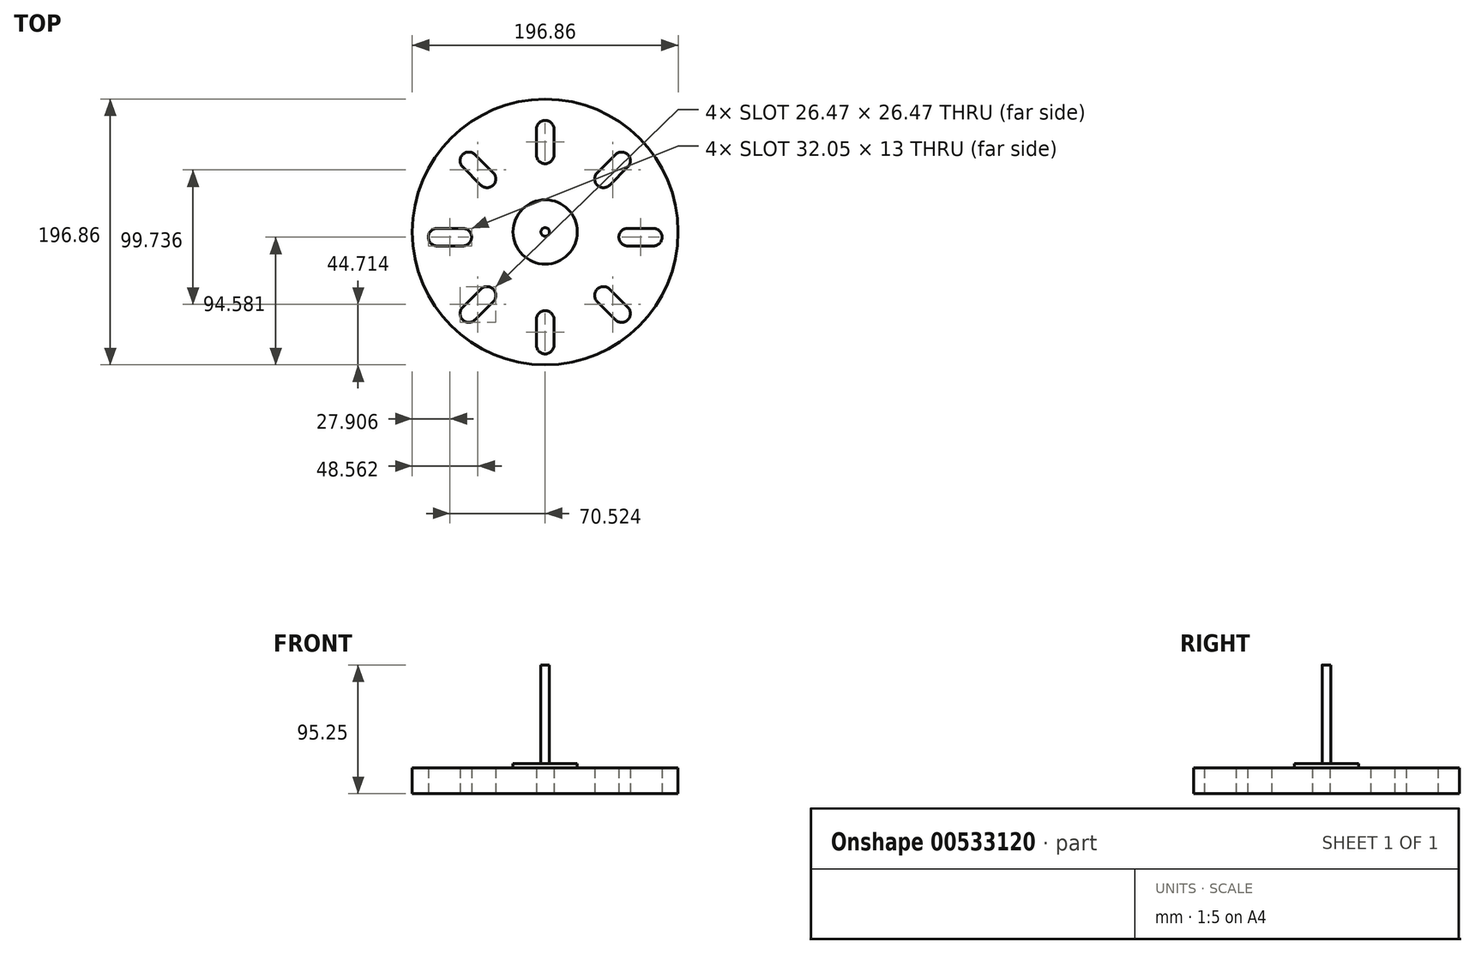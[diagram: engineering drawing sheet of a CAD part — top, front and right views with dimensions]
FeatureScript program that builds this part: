
annotation { "Feature Type Name" : "Feature", "Feature Type Description" : "" }
export const myFeature = defineFeature(function(context is Context, id is Id, definition is map)
    precondition{}
    {
        {
            var Q0;
            Q0=qCreatedBy(makeId("Top.planeOp"),FACE);
            var sketch = newSketch(context, id + "F0", { "sketchPlane" : qUnion([Q0])});
            skCircle(sketch, "E0", {"center": v(0, 0) * mm, "radius": 20.64 * mm});
            skCircle(sketch, "E1", {"center": v(0, 0) * mm, "radius": 98.43 * mm});
            skCircle(sketch, "E2", {"center": v(0, 0) * mm, "radius": 66.68 * mm, "construction": true});
            skPoint(sketch, "E3.center", {"position": v(-3.85, -3.85) * mm});
            skLineSegment(sketch, "E4", {"start": v(0, 57.15) * mm, "end": v(0, 76.2) * mm});
            skLineSegment(sketch, "E5.1.0", {"start": v(-43.13, 39.28) * mm, "end": v(-56.6, 52.75) * mm});
            skLineSegment(sketch, "E5.2.0", {"start": v(-61, -3.85) * mm, "end": v(-80.05, -3.85) * mm});
            skLineSegment(sketch, "E5.3.0", {"start": v(-43.13, -46.98) * mm, "end": v(-56.6, -60.45) * mm});
            skLineSegment(sketch, "E5.4.0", {"start": v(0, -64.85) * mm, "end": v(0, -83.9) * mm});
            skLineSegment(sketch, "E5.5.0", {"start": v(43.13, -46.98) * mm, "end": v(56.6, -60.45) * mm});
            skLineSegment(sketch, "E5.6.0", {"start": v(61, -3.85) * mm, "end": v(80.05, -3.85) * mm});
            skLineSegment(sketch, "E5.7.0", {"start": v(43.13, 39.28) * mm, "end": v(56.6, 52.75) * mm});
            skPoint(sketch, "E5.center", {"position": v(0, -3.85) * mm});
            skArc(sketch, "E6.0.startCap", {"start": v(6.5, 57.15) * mm, "mid": v(0, 50.65) * mm, "end": v(-6.5, 57.15) * mm});
            skArc(sketch, "E6.0.endCap", {"start": v(-6.5, 76.2) * mm, "mid": v(0, 82.7) * mm, "end": v(6.5, 76.2) * mm});
            skLineSegment(sketch, "E6.0.left", {"start": v(-6.5, 57.15) * mm, "end": v(-6.5, 76.2) * mm});
            skLineSegment(sketch, "E6.0.right", {"start": v(6.5, 57.15) * mm, "end": v(6.5, 76.2) * mm});
            skArc(sketch, "E6.1.startCap", {"start": v(47.73, 34.69) * mm, "mid": v(38.54, 34.69) * mm, "end": v(38.54, 43.88) * mm});
            skArc(sketch, "E6.1.endCap", {"start": v(52, 57.35) * mm, "mid": v(61.2, 57.35) * mm, "end": v(61.2, 48.16) * mm});
            skLineSegment(sketch, "E6.1.left", {"start": v(38.54, 43.88) * mm, "end": v(52, 57.35) * mm});
            skLineSegment(sketch, "E6.1.right", {"start": v(47.73, 34.69) * mm, "end": v(61.2, 48.16) * mm});
            skArc(sketch, "E6.2.startCap", {"start": v(47.73, 34.69) * mm, "mid": v(38.54, 34.69) * mm, "end": v(38.54, 43.88) * mm});
            skArc(sketch, "E6.2.endCap", {"start": v(52, 57.35) * mm, "mid": v(61.2, 57.35) * mm, "end": v(61.2, 48.16) * mm});
            skLineSegment(sketch, "E6.2.left", {"start": v(38.54, 43.88) * mm, "end": v(52, 57.35) * mm});
            skLineSegment(sketch, "E6.2.right", {"start": v(47.73, 34.69) * mm, "end": v(61.2, 48.16) * mm});
            skArc(sketch, "E6.3.startCap", {"start": v(61, -10.35) * mm, "mid": v(54.5, -3.85) * mm, "end": v(61, 2.65) * mm});
            skArc(sketch, "E6.3.endCap", {"start": v(80.05, 2.65) * mm, "mid": v(86.55, -3.85) * mm, "end": v(80.05, -10.35) * mm});
            skLineSegment(sketch, "E6.3.left", {"start": v(61, 2.65) * mm, "end": v(80.05, 2.65) * mm});
            skLineSegment(sketch, "E6.3.right", {"start": v(61, -10.35) * mm, "end": v(80.05, -10.35) * mm});
            skArc(sketch, "E6.4.startCap", {"start": v(38.54, -51.58) * mm, "mid": v(38.54, -42.39) * mm, "end": v(47.73, -42.39) * mm});
            skArc(sketch, "E6.4.endCap", {"start": v(61.2, -55.86) * mm, "mid": v(61.2, -65.05) * mm, "end": v(52, -65.05) * mm});
            skLineSegment(sketch, "E6.4.left", {"start": v(47.73, -42.39) * mm, "end": v(61.2, -55.86) * mm});
            skLineSegment(sketch, "E6.4.right", {"start": v(38.54, -51.58) * mm, "end": v(52, -65.05) * mm});
            skArc(sketch, "E6.5.startCap", {"start": v(-6.5, -64.85) * mm, "mid": v(0, -58.35) * mm, "end": v(6.5, -64.85) * mm});
            skArc(sketch, "E6.5.endCap", {"start": v(6.5, -83.9) * mm, "mid": v(0, -90.4) * mm, "end": v(-6.5, -83.9) * mm});
            skLineSegment(sketch, "E6.5.left", {"start": v(6.5, -64.85) * mm, "end": v(6.5, -83.9) * mm});
            skLineSegment(sketch, "E6.5.right", {"start": v(-6.5, -64.85) * mm, "end": v(-6.5, -83.9) * mm});
            skArc(sketch, "E6.6.startCap", {"start": v(-47.73, -42.39) * mm, "mid": v(-38.54, -42.39) * mm, "end": v(-38.54, -51.58) * mm});
            skArc(sketch, "E6.6.endCap", {"start": v(-52, -65.05) * mm, "mid": v(-61.2, -65.05) * mm, "end": v(-61.2, -55.86) * mm});
            skLineSegment(sketch, "E6.6.left", {"start": v(-38.54, -51.58) * mm, "end": v(-52, -65.05) * mm});
            skLineSegment(sketch, "E6.6.right", {"start": v(-47.73, -42.39) * mm, "end": v(-61.2, -55.86) * mm});
            skArc(sketch, "E6.7.startCap", {"start": v(-61, 2.65) * mm, "mid": v(-54.5, -3.85) * mm, "end": v(-61, -10.35) * mm});
            skArc(sketch, "E6.7.endCap", {"start": v(-80.05, -10.35) * mm, "mid": v(-86.55, -3.85) * mm, "end": v(-80.05, 2.65) * mm});
            skLineSegment(sketch, "E6.7.left", {"start": v(-61, -10.35) * mm, "end": v(-80.05, -10.35) * mm});
            skLineSegment(sketch, "E6.7.right", {"start": v(-61, 2.65) * mm, "end": v(-80.05, 2.65) * mm});
            skArc(sketch, "E6.8.startCap", {"start": v(-38.54, 43.88) * mm, "mid": v(-38.54, 34.69) * mm, "end": v(-47.73, 34.69) * mm});
            skArc(sketch, "E6.8.endCap", {"start": v(-61.2, 48.16) * mm, "mid": v(-61.2, 57.35) * mm, "end": v(-52, 57.35) * mm});
            skLineSegment(sketch, "E6.8.left", {"start": v(-47.73, 34.69) * mm, "end": v(-61.2, 48.16) * mm});
            skLineSegment(sketch, "E6.8.right", {"start": v(-38.54, 43.88) * mm, "end": v(-52, 57.35) * mm});
            skSolve(sketch);
        }
        {
            var Q0;
            Q0=makeQuery(id+"F0.imprint","IMPRINT",FACE,{"disambiguationData":[TD([[makeQuery(id+"F0.imprint","IMPRINT",EDGE,{"derivedFrom":sQuery(id+"F0.wireOp",EDGE,"E0")}),-1.0]])]});
            extrude(context, id + "F1", {"entities" : qUnion([Q0]), "depth" : 19.05 * mm, "offsetDistance" : 25.4 * mm});
        }
        {
            var Q0;
            Q0=makeQuery(id+"F1.opExtrude","CAP_FACE",FACE,{"disambiguationData":[OSD([sQuery(id+"F0.wireOp",EDGE,"E0"),sQuery(id+"F0.wireOp",EDGE,"E1"),sQuery(id+"F0.wireOp",EDGE,"E6.0.startCap"),sQuery(id+"F0.wireOp",EDGE,"E6.0.endCap"),sQuery(id+"F0.wireOp",EDGE,"E6.0.left"),sQuery(id+"F0.wireOp",EDGE,"E6.0.right"),sQuery(id+"F0.wireOp",EDGE,"E6.2.startCap"),sQuery(id+"F0.wireOp",EDGE,"E6.2.endCap"),sQuery(id+"F0.wireOp",EDGE,"E6.2.left"),sQuery(id+"F0.wireOp",EDGE,"E6.2.right"),sQuery(id+"F0.wireOp",EDGE,"E6.3.startCap"),sQuery(id+"F0.wireOp",EDGE,"E6.3.endCap"),sQuery(id+"F0.wireOp",EDGE,"E6.3.left"),sQuery(id+"F0.wireOp",EDGE,"E6.3.right"),sQuery(id+"F0.wireOp",EDGE,"E6.4.startCap"),sQuery(id+"F0.wireOp",EDGE,"E6.4.endCap"),sQuery(id+"F0.wireOp",EDGE,"E6.4.left"),sQuery(id+"F0.wireOp",EDGE,"E6.4.right"),sQuery(id+"F0.wireOp",EDGE,"E6.5.startCap"),sQuery(id+"F0.wireOp",EDGE,"E6.5.endCap"),sQuery(id+"F0.wireOp",EDGE,"E6.5.left"),sQuery(id+"F0.wireOp",EDGE,"E6.5.right"),sQuery(id+"F0.wireOp",EDGE,"E6.6.startCap"),sQuery(id+"F0.wireOp",EDGE,"E6.6.endCap"),sQuery(id+"F0.wireOp",EDGE,"E6.6.left"),sQuery(id+"F0.wireOp",EDGE,"E6.6.right"),sQuery(id+"F0.wireOp",EDGE,"E6.7.startCap"),sQuery(id+"F0.wireOp",EDGE,"E6.7.endCap"),sQuery(id+"F0.wireOp",EDGE,"E6.7.left"),sQuery(id+"F0.wireOp",EDGE,"E6.7.right"),sQuery(id+"F0.wireOp",EDGE,"E6.8.startCap"),sQuery(id+"F0.wireOp",EDGE,"E6.8.endCap"),sQuery(id+"F0.wireOp",EDGE,"E6.8.left"),sQuery(id+"F0.wireOp",EDGE,"E6.8.right")])],"isStart":false});
            var sketch = newSketch(context, id + "F2", { "sketchPlane" : qUnion([Q0])});
            skCircle(sketch, "E7.0", {"center": v(0, 0) * mm, "radius": 20.64 * mm});
            skCircle(sketch, "E8", {"center": v(0, 0) * mm, "radius": 23.81 * mm});
            skSolve(sketch);
        }
        {
            var Q0;
            Q0=makeQuery(id+"F2.imprint","IMPRINT",FACE,{"disambiguationData":[TD([[makeQuery(id+"F2.imprint","IMPRINT",EDGE,{"derivedFrom":sQuery(id+"F2.wireOp",EDGE,"E7.0")}),1.0]])]});
            var Q1;
            Q1=makeQuery(id+"F1.opExtrude","CAP_FACE",FACE,{"disambiguationData":[OSD([sQuery(id+"F0.wireOp",EDGE,"E0"),sQuery(id+"F0.wireOp",EDGE,"E1"),sQuery(id+"F0.wireOp",EDGE,"E6.0.startCap"),sQuery(id+"F0.wireOp",EDGE,"E6.0.endCap"),sQuery(id+"F0.wireOp",EDGE,"E6.0.left"),sQuery(id+"F0.wireOp",EDGE,"E6.0.right"),sQuery(id+"F0.wireOp",EDGE,"E6.2.startCap"),sQuery(id+"F0.wireOp",EDGE,"E6.2.endCap"),sQuery(id+"F0.wireOp",EDGE,"E6.2.left"),sQuery(id+"F0.wireOp",EDGE,"E6.2.right"),sQuery(id+"F0.wireOp",EDGE,"E6.3.startCap"),sQuery(id+"F0.wireOp",EDGE,"E6.3.endCap"),sQuery(id+"F0.wireOp",EDGE,"E6.3.left"),sQuery(id+"F0.wireOp",EDGE,"E6.3.right"),sQuery(id+"F0.wireOp",EDGE,"E6.4.startCap"),sQuery(id+"F0.wireOp",EDGE,"E6.4.endCap"),sQuery(id+"F0.wireOp",EDGE,"E6.4.left"),sQuery(id+"F0.wireOp",EDGE,"E6.4.right"),sQuery(id+"F0.wireOp",EDGE,"E6.5.startCap"),sQuery(id+"F0.wireOp",EDGE,"E6.5.endCap"),sQuery(id+"F0.wireOp",EDGE,"E6.5.left"),sQuery(id+"F0.wireOp",EDGE,"E6.5.right"),sQuery(id+"F0.wireOp",EDGE,"E6.6.startCap"),sQuery(id+"F0.wireOp",EDGE,"E6.6.endCap"),sQuery(id+"F0.wireOp",EDGE,"E6.6.left"),sQuery(id+"F0.wireOp",EDGE,"E6.6.right"),sQuery(id+"F0.wireOp",EDGE,"E6.7.startCap"),sQuery(id+"F0.wireOp",EDGE,"E6.7.endCap"),sQuery(id+"F0.wireOp",EDGE,"E6.7.left"),sQuery(id+"F0.wireOp",EDGE,"E6.7.right"),sQuery(id+"F0.wireOp",EDGE,"E6.8.startCap"),sQuery(id+"F0.wireOp",EDGE,"E6.8.endCap"),sQuery(id+"F0.wireOp",EDGE,"E6.8.left"),sQuery(id+"F0.wireOp",EDGE,"E6.8.right")])],"isStart":true});
            extrude(context, id + "F3", {"entities" : qUnion([Q0]), "endBound" : BoundingType.UP_TO_SURFACE, "oppositeDirection" : true, "depth" : 25.4 * mm, "endBoundEntityFace" : qUnion([Q1]), "offsetDistance" : 25.4 * mm});
        }
        {
            var Q0;
            Q0=makeQuery(id+"F3.opExtrude","CAP_FACE",FACE,{"disambiguationData":[OSD([sQuery(id+"F2.wireOp",EDGE,"E7.0")])],"isStart":true});
            var sketch = newSketch(context, id + "F4", { "sketchPlane" : qUnion([Q0])});
            skPoint(sketch, "E9.0", {"position": v(0, 0) * mm});
            skCircle(sketch, "E10", {"center": v(0, 0) * mm, "radius": 3.18 * mm});
            skSolve(sketch);
        }
        {
            var Q0;
            Q0 = qSketchRegion(id + "F4", true);
            extrude(context, id + "F5", {"entities" : qUnion([Q0]), "operationType" : NewBodyOperationType.ADD, "depth" : 76.2 * mm, "offsetDistance" : 25.4 * mm});
        }
        {
            var Q0;
            Q0=makeQuery(id+"F2.imprint","IMPRINT",FACE,{"disambiguationData":[TD([[makeQuery(id+"F2.imprint","IMPRINT",EDGE,{"derivedFrom":sQuery(id+"F2.wireOp",EDGE,"E7.0")}),-1.0]])]});
            var Q1;
            Q1=makeQuery(id+"F2.imprint","IMPRINT",FACE,{"disambiguationData":[TD([[makeQuery(id+"F2.imprint","IMPRINT",EDGE,{"derivedFrom":sQuery(id+"F2.wireOp",EDGE,"E7.0")}),1.0]])]});
            extrude(context, id + "F6", {"entities" : qUnion([Q0, Q1]), "operationType" : NewBodyOperationType.ADD, "depth" : 3.17 * mm, "offsetDistance" : 25.4 * mm});
        }
    });
